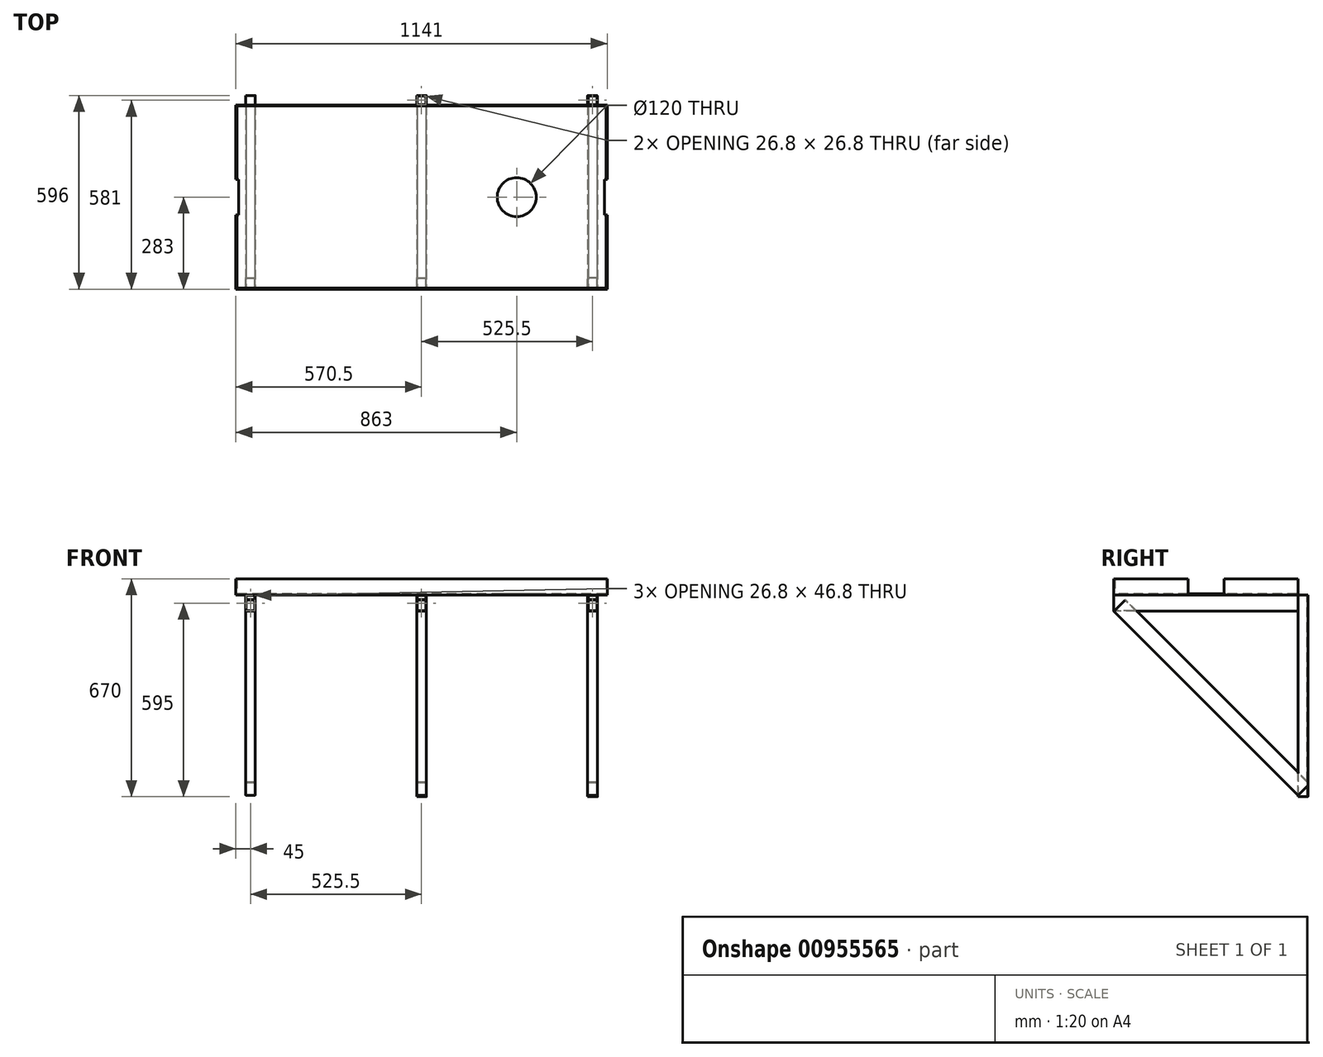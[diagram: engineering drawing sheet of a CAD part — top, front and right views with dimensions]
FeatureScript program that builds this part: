
annotation { "Feature Type Name" : "Feature", "Feature Type Description" : "" }
export const myFeature = defineFeature(function(context is Context, id is Id, definition is map)
    precondition{}
    {
        {
            var Q0;
            Q0=qCreatedBy(makeId("Top.planeOp"),FACE);
            var sketch = newSketch(context, id + "F0", { "sketchPlane" : qUnion([Q0])});
            skLineSegment(sketch, "E0.bottom", {"start": v(567.5, 280) * mm, "end": v(-567.5, 280) * mm});
            skLineSegment(sketch, "E0.top", {"start": v(567.5, -280) * mm, "end": v(-567.5, -280) * mm});
            skLineSegment(sketch, "E0.left", {"start": v(567.5, 280) * mm, "end": v(567.5, -280) * mm});
            skLineSegment(sketch, "E0.right", {"start": v(-567.5, 280) * mm, "end": v(-567.5, -280) * mm});
            skPoint(sketch, "E0.middle", {"position": v(0, 0) * mm});
            skLineSegment(sketch, "E1.0", {"start": v(570.5, 283) * mm, "end": v(-570.5, 283) * mm});
            skLineSegment(sketch, "E1.1", {"start": v(570.5, 283) * mm, "end": v(570.5, -283) * mm});
            skLineSegment(sketch, "E1.2", {"start": v(570.5, -283) * mm, "end": v(-570.5, -283) * mm});
            skLineSegment(sketch, "E1.3", {"start": v(-570.5, 283) * mm, "end": v(-570.5, -283) * mm});
            skLineSegment(sketch, "E2.bottom", {"start": v(567.5, 55) * mm, "end": v(-567.5, 55) * mm, "construction": true});
            skLineSegment(sketch, "E2.top", {"start": v(567.5, -55) * mm, "end": v(-567.5, -55) * mm, "construction": true});
            skLineSegment(sketch, "E2.left", {"start": v(567.5, 55) * mm, "end": v(567.5, -55) * mm, "construction": true});
            skLineSegment(sketch, "E2.right", {"start": v(-567.5, 55) * mm, "end": v(-567.5, -55) * mm, "construction": true});
            skLineSegment(sketch, "E3.bottom", {"start": v(-567.5, -55) * mm, "end": v(-562.5, -55) * mm});
            skLineSegment(sketch, "E3.top", {"start": v(-567.5, 55) * mm, "end": v(-562.5, 55) * mm});
            skLineSegment(sketch, "E3.left", {"start": v(-567.5, -55) * mm, "end": v(-567.5, 55) * mm});
            skLineSegment(sketch, "E3.right", {"start": v(-562.5, -55) * mm, "end": v(-562.5, 55) * mm});
            skLineSegment(sketch, "E4.MirrorCS", {"start": v(562.5, -55) * mm, "end": v(562.5, 55) * mm});
            skLineSegment(sketch, "E5", {"start": v(-567.5, -55) * mm, "end": v(-570.5, -55) * mm});
            skLineSegment(sketch, "E6", {"start": v(-567.5, 55) * mm, "end": v(-570.5, 55) * mm});
            skLineSegment(sketch, "E7.MirrorCS", {"start": v(567.5, -55) * mm, "end": v(570.5, -55) * mm});
            skLineSegment(sketch, "E8.MirrorCS", {"start": v(567.5, 55) * mm, "end": v(570.5, 55) * mm});
            skLineSegment(sketch, "E9", {"start": v(562.5, -55) * mm, "end": v(567.5, -55) * mm});
            skLineSegment(sketch, "E10", {"start": v(562.5, 55) * mm, "end": v(567.5, 55) * mm});
            skLineSegment(sketch, "E11", {"start": v(-567.5, 0) * mm, "end": v(562.5, 0) * mm, "construction": true});
            skCircle(sketch, "E12", {"center": v(292.5, 0) * mm, "radius": 60 * mm});
            skPoint(sketch, "E13", {"position": v(-540.5, 283) * mm});
            skLineSegment(sketch, "E14.bottom", {"start": v(-538.5, 283) * mm, "end": v(-512.5, 283) * mm});
            skLineSegment(sketch, "E14.top", {"start": v(-538.5, 313) * mm, "end": v(-512.5, 313) * mm});
            skLineSegment(sketch, "E14.left", {"start": v(-540.5, 285) * mm, "end": v(-540.5, 311) * mm});
            skLineSegment(sketch, "E14.right", {"start": v(-510.5, 285) * mm, "end": v(-510.5, 311) * mm});
            skLineSegment(sketch, "E15.0", {"start": v(-538.9, 286.6) * mm, "end": v(-538.9, 309.4) * mm});
            skLineSegment(sketch, "E15.1", {"start": v(-536.9, 311.4) * mm, "end": v(-514.1, 311.4) * mm});
            skLineSegment(sketch, "E15.2", {"start": v(-512.1, 286.6) * mm, "end": v(-512.1, 309.4) * mm});
            skLineSegment(sketch, "E16", {"start": v(-536.9, 284.6) * mm, "end": v(-514.1, 284.6) * mm});
            skPoint(sketch, "E17.visualSharp", {"position": v(-538.9, 311.4) * mm});
            skArc(sketch, "E17.filletArc", {"start": v(-536.9, 311.4) * mm, "mid": v(-538.31, 310.81) * mm, "end": v(-538.9, 309.4) * mm});
            skPoint(sketch, "E18.visualSharp", {"position": v(-512.1, 311.4) * mm});
            skArc(sketch, "E18.filletArc", {"start": v(-512.1, 309.4) * mm, "mid": v(-512.69, 310.81) * mm, "end": v(-514.1, 311.4) * mm});
            skPoint(sketch, "E19.visualSharp", {"position": v(-512.1, 284.6) * mm});
            skArc(sketch, "E19.filletArc", {"start": v(-514.1, 284.6) * mm, "mid": v(-512.69, 285.19) * mm, "end": v(-512.1, 286.6) * mm});
            skPoint(sketch, "E20.visualSharp", {"position": v(-538.9, 284.6) * mm});
            skArc(sketch, "E20.filletArc", {"start": v(-538.9, 286.6) * mm, "mid": v(-538.31, 285.19) * mm, "end": v(-536.9, 284.6) * mm});
            skPoint(sketch, "E21.visualSharp", {"position": v(-540.5, 313) * mm});
            skArc(sketch, "E21.filletArc", {"start": v(-538.5, 313) * mm, "mid": v(-539.91, 312.41) * mm, "end": v(-540.5, 311) * mm});
            skPoint(sketch, "E22.visualSharp", {"position": v(-510.5, 313) * mm});
            skArc(sketch, "E22.filletArc", {"start": v(-510.5, 311) * mm, "mid": v(-511.09, 312.41) * mm, "end": v(-512.5, 313) * mm});
            skPoint(sketch, "E23.visualSharp", {"position": v(-510.5, 283) * mm});
            skArc(sketch, "E23.filletArc", {"start": v(-512.5, 283) * mm, "mid": v(-511.09, 283.59) * mm, "end": v(-510.5, 285) * mm});
            skArc(sketch, "E24.filletArc", {"start": v(-540.5, 285) * mm, "mid": v(-539.91, 283.59) * mm, "end": v(-538.5, 283) * mm});
            skLineSegment(sketch, "E25.MirrorCS", {"start": v(538.5, 313) * mm, "end": v(512.5, 313) * mm});
            skLineSegment(sketch, "E26.MirrorCS", {"start": v(536.9, 311.4) * mm, "end": v(514.1, 311.4) * mm});
            skLineSegment(sketch, "E27.MirrorCS", {"start": v(536.9, 284.6) * mm, "end": v(514.1, 284.6) * mm});
            skLineSegment(sketch, "E28.MirrorCS", {"start": v(510.5, 285) * mm, "end": v(510.5, 311) * mm});
            skLineSegment(sketch, "E29.MirrorCS", {"start": v(512.1, 286.6) * mm, "end": v(512.1, 309.4) * mm});
            skLineSegment(sketch, "E30.MirrorCS", {"start": v(538.9, 286.6) * mm, "end": v(538.9, 309.4) * mm});
            skLineSegment(sketch, "E31.MirrorCS", {"start": v(540.5, 285) * mm, "end": v(540.5, 311) * mm});
            skArc(sketch, "E32.MirrorCS", {"start": v(512.1, 309.4) * mm, "mid": v(512.69, 310.81) * mm, "end": v(514.1, 311.4) * mm});
            skArc(sketch, "E33.MirrorCS", {"start": v(510.5, 311) * mm, "mid": v(511.09, 312.41) * mm, "end": v(512.5, 313) * mm});
            skArc(sketch, "E34.MirrorCS", {"start": v(536.9, 311.4) * mm, "mid": v(538.31, 310.81) * mm, "end": v(538.9, 309.4) * mm});
            skArc(sketch, "E35.MirrorCS", {"start": v(538.5, 313) * mm, "mid": v(539.91, 312.41) * mm, "end": v(540.5, 311) * mm});
            skArc(sketch, "E36.MirrorCS", {"start": v(512.5, 283) * mm, "mid": v(511.09, 283.59) * mm, "end": v(510.5, 285) * mm});
            skArc(sketch, "E37.MirrorCS", {"start": v(514.1, 284.6) * mm, "mid": v(512.69, 285.19) * mm, "end": v(512.1, 286.6) * mm});
            skArc(sketch, "E38.MirrorCS", {"start": v(538.9, 286.6) * mm, "mid": v(538.31, 285.19) * mm, "end": v(536.9, 284.6) * mm});
            skArc(sketch, "E39.MirrorCS", {"start": v(540.5, 285) * mm, "mid": v(539.91, 283.59) * mm, "end": v(538.5, 283) * mm});
            skLineSegment(sketch, "E40.1.0.0", {"start": v(-13, 313) * mm, "end": v(13, 313) * mm});
            skPoint(sketch, "E40.1.0.1", {"position": v(-13.4, 284.6) * mm});
            skLineSegment(sketch, "E40.1.0.2", {"start": v(13.4, 286.6) * mm, "end": v(13.4, 309.4) * mm});
            skLineSegment(sketch, "E40.1.0.3", {"start": v(-13.4, 286.6) * mm, "end": v(-13.4, 309.4) * mm});
            skPoint(sketch, "E40.1.0.4", {"position": v(13.4, 284.6) * mm});
            skPoint(sketch, "E40.1.0.5", {"position": v(-15, 313) * mm});
            skLineSegment(sketch, "E40.1.0.6", {"start": v(-15, 285) * mm, "end": v(-15, 311) * mm});
            skPoint(sketch, "E40.1.0.7", {"position": v(13.4, 311.4) * mm});
            skLineSegment(sketch, "E40.1.0.8", {"start": v(-11.4, 284.6) * mm, "end": v(11.4, 284.6) * mm});
            skPoint(sketch, "E40.1.0.9", {"position": v(15, 313) * mm});
            skLineSegment(sketch, "E40.1.0.10", {"start": v(15, 285) * mm, "end": v(15, 311) * mm});
            skLineSegment(sketch, "E40.1.0.11", {"start": v(-13, 283) * mm, "end": v(13, 283) * mm});
            skLineSegment(sketch, "E40.1.0.12", {"start": v(-11.4, 311.4) * mm, "end": v(11.4, 311.4) * mm});
            skPoint(sketch, "E40.1.0.13", {"position": v(-13.4, 311.4) * mm});
            skArc(sketch, "E40.1.0.14", {"start": v(13.4, 309.4) * mm, "mid": v(12.81, 310.81) * mm, "end": v(11.4, 311.4) * mm});
            skArc(sketch, "E40.1.0.15", {"start": v(15, 311) * mm, "mid": v(14.41, 312.41) * mm, "end": v(13, 313) * mm});
            skArc(sketch, "E40.1.0.16", {"start": v(-13, 313) * mm, "mid": v(-14.41, 312.41) * mm, "end": v(-15, 311) * mm});
            skArc(sketch, "E40.1.0.17", {"start": v(-13.4, 286.6) * mm, "mid": v(-12.81, 285.19) * mm, "end": v(-11.4, 284.6) * mm});
            skArc(sketch, "E40.1.0.18", {"start": v(-15, 285) * mm, "mid": v(-14.41, 283.59) * mm, "end": v(-13, 283) * mm});
            skArc(sketch, "E40.1.0.19", {"start": v(11.4, 284.6) * mm, "mid": v(12.81, 285.19) * mm, "end": v(13.4, 286.6) * mm});
            skArc(sketch, "E40.1.0.20", {"start": v(-11.4, 311.4) * mm, "mid": v(-12.81, 310.81) * mm, "end": v(-13.4, 309.4) * mm});
            skArc(sketch, "E40.1.0.21", {"start": v(13, 283) * mm, "mid": v(14.41, 283.59) * mm, "end": v(15, 285) * mm});
            skLineSegment(sketch, "E40.direction1", {"start": v(-538.5, 283) * mm, "end": v(-13, 283) * mm, "construction": true});
            skPoint(sketch, "E41", {"position": v(525.5, 284.6) * mm});
            skLineSegment(sketch, "E42.bottom", {"start": v(-540.5, 313) * mm, "end": v(-510.5, 313) * mm});
            skLineSegment(sketch, "E42.top", {"start": v(-540.5, 333) * mm, "end": v(-510.5, 333) * mm});
            skLineSegment(sketch, "E42.left", {"start": v(-540.5, 313) * mm, "end": v(-540.5, 333) * mm});
            skLineSegment(sketch, "E42.right", {"start": v(-510.5, 313) * mm, "end": v(-510.5, 333) * mm});
            skLineSegment(sketch, "E43.MirrorCS", {"start": v(540.5, 333) * mm, "end": v(510.5, 333) * mm});
            skLineSegment(sketch, "E44.MirrorCS", {"start": v(510.5, 313) * mm, "end": v(510.5, 333) * mm});
            skLineSegment(sketch, "E45.MirrorCS", {"start": v(540.5, 313) * mm, "end": v(540.5, 333) * mm});
            skLineSegment(sketch, "E46.MirrorCS", {"start": v(540.5, 313) * mm, "end": v(510.5, 313) * mm});
            skLineSegment(sketch, "E47.bottom", {"start": v(-15, 313) * mm, "end": v(15, 313) * mm});
            skLineSegment(sketch, "E47.top", {"start": v(-15, 333) * mm, "end": v(15, 333) * mm});
            skLineSegment(sketch, "E47.left", {"start": v(-15, 313) * mm, "end": v(-15, 333) * mm});
            skLineSegment(sketch, "E47.right", {"start": v(15, 313) * mm, "end": v(15, 333) * mm});
            skSolve(sketch);
        }
        {
            var Q0;
            Q0=makeQuery(id+"F0.imprint","IMPRINT",FACE,{"disambiguationData":[TD([[makeQuery(id+"F0.imprint","IMPRINT",EDGE,{"derivedFrom":sQuery(id+"F0.wireOp",EDGE,"E0.bottom")}),1.0]])]});
            extrude(context, id + "F1", {"entities" : qUnion([Q0]), "depth" : 4 * mm, "offsetDistance" : 25 * mm});
        }
        {
            var Q0;
            Q0=makeQuery(id+"F0.imprint","IMPRINT",FACE,{"disambiguationData":[TD([[makeQuery(id+"F0.imprint","IMPRINT",EDGE,{"derivedFrom":sQuery(id+"F0.wireOp",EDGE,"E0.bottom")}),-1.0]])]});
            var Q1;
            {var subQ4=sQuery(id+"F0.wireOp",EDGE,"E0.top");Q1=makeQuery(id+"F0.imprint","IMPRINT",FACE,{"disambiguationData":[TD([[makeQuery(id+"F0.imprint","IMPRINT",EDGE,{"derivedFrom":subQ4}),1.0]])]});}
            extrude(context, id + "F2", {"entities" : qUnion([Q0, Q1]), "operationType" : NewBodyOperationType.ADD, "depth" : 50 * mm, "offsetDistance" : 25 * mm});
        }
        {
            var Q0;
            Q0=makeQuery(id+"F2.opExtrude","SWEPT_FACE",FACE,{"disambiguationData":[OSD([sQuery(id+"F0.wireOp",EDGE,"E1.2")])]});
            var sketch = newSketch(context, id + "F3", { "sketchPlane" : qUnion([Q0])});
            skPoint(sketch, "E48", {"position": v(-540.5, 0) * mm});
            skLineSegment(sketch, "E49.bottom", {"start": v(-538.5, 0) * mm, "end": v(-512.5, 0) * mm});
            skLineSegment(sketch, "E49.top", {"start": v(-538.5, -50) * mm, "end": v(-512.5, -50) * mm});
            skLineSegment(sketch, "E49.left", {"start": v(-540.5, -2) * mm, "end": v(-540.5, -48) * mm});
            skLineSegment(sketch, "E49.right", {"start": v(-510.5, -2) * mm, "end": v(-510.5, -48) * mm});
            skLineSegment(sketch, "E50.MirrorCS", {"start": v(538.5, -50) * mm, "end": v(512.5, -50) * mm});
            skLineSegment(sketch, "E51.MirrorCS", {"start": v(540.5, -2) * mm, "end": v(540.5, -48) * mm});
            skLineSegment(sketch, "E52.MirrorCS", {"start": v(510.5, -2) * mm, "end": v(510.5, -48) * mm});
            skLineSegment(sketch, "E53.MirrorCS", {"start": v(538.5, 0) * mm, "end": v(512.5, 0) * mm});
            skPoint(sketch, "E54", {"position": v(-15, 0) * mm});
            skLineSegment(sketch, "E55.bottom", {"start": v(-13, 0) * mm, "end": v(13, 0) * mm});
            skLineSegment(sketch, "E55.top", {"start": v(-13, -50) * mm, "end": v(13, -50) * mm});
            skLineSegment(sketch, "E55.left", {"start": v(-15, -2) * mm, "end": v(-15, -48) * mm});
            skLineSegment(sketch, "E55.right", {"start": v(15, -2) * mm, "end": v(15, -48) * mm});
            skPoint(sketch, "E56.visualSharp", {"position": v(-510.5, -50) * mm});
            skArc(sketch, "E56.filletArc", {"start": v(-512.5, -50) * mm, "mid": v(-511.09, -49.41) * mm, "end": v(-510.5, -48) * mm});
            skPoint(sketch, "E57.visualSharp", {"position": v(-540.5, -50) * mm});
            skArc(sketch, "E57.filletArc", {"start": v(-540.5, -48) * mm, "mid": v(-539.91, -49.41) * mm, "end": v(-538.5, -50) * mm});
            skPoint(sketch, "E58.visualSharp", {"position": v(-510.5, 0) * mm});
            skArc(sketch, "E58.filletArc", {"start": v(-510.5, -2) * mm, "mid": v(-511.09, -0.59) * mm, "end": v(-512.5, 0) * mm});
            skArc(sketch, "E59.filletArc", {"start": v(-538.5, 0) * mm, "mid": v(-539.91, -0.59) * mm, "end": v(-540.5, -2) * mm});
            skPoint(sketch, "E60.visualSharp", {"position": v(540.5, 0) * mm});
            skArc(sketch, "E60.filletArc", {"start": v(540.5, -2) * mm, "mid": v(539.91, -0.59) * mm, "end": v(538.5, 0) * mm});
            skPoint(sketch, "E61.visualSharp", {"position": v(510.5, 0) * mm});
            skArc(sketch, "E61.filletArc", {"start": v(512.5, 0) * mm, "mid": v(511.09, -0.59) * mm, "end": v(510.5, -2) * mm});
            skPoint(sketch, "E62.visualSharp", {"position": v(510.5, -50) * mm});
            skArc(sketch, "E62.filletArc", {"start": v(510.5, -48) * mm, "mid": v(511.09, -49.41) * mm, "end": v(512.5, -50) * mm});
            skPoint(sketch, "E63.visualSharp", {"position": v(540.5, -50) * mm});
            skArc(sketch, "E63.filletArc", {"start": v(538.5, -50) * mm, "mid": v(539.91, -49.41) * mm, "end": v(540.5, -48) * mm});
            skPoint(sketch, "E64.visualSharp", {"position": v(-15, -50) * mm});
            skArc(sketch, "E64.filletArc", {"start": v(-15, -48) * mm, "mid": v(-14.41, -49.41) * mm, "end": v(-13, -50) * mm});
            skPoint(sketch, "E65.visualSharp", {"position": v(15, -50) * mm});
            skArc(sketch, "E65.filletArc", {"start": v(13, -50) * mm, "mid": v(14.41, -49.41) * mm, "end": v(15, -48) * mm});
            skPoint(sketch, "E66.visualSharp", {"position": v(15, 0) * mm});
            skArc(sketch, "E66.filletArc", {"start": v(15, -2) * mm, "mid": v(14.41, -0.59) * mm, "end": v(13, 0) * mm});
            skArc(sketch, "E67.filletArc", {"start": v(-13, 0) * mm, "mid": v(-14.41, -0.59) * mm, "end": v(-15, -2) * mm});
            skLineSegment(sketch, "E68.0", {"start": v(-538.9, -2) * mm, "end": v(-538.9, -48) * mm});
            skArc(sketch, "E69.0", {"start": v(-538.9, -48) * mm, "mid": v(-538.78, -48.28) * mm, "end": v(-538.5, -48.4) * mm});
            skLineSegment(sketch, "E70.0", {"start": v(-538.5, -48.4) * mm, "end": v(-512.5, -48.4) * mm});
            skArc(sketch, "E71.0", {"start": v(-512.5, -48.4) * mm, "mid": v(-512.22, -48.28) * mm, "end": v(-512.1, -48) * mm});
            skLineSegment(sketch, "E72.0", {"start": v(-512.1, -2) * mm, "end": v(-512.1, -48) * mm});
            skArc(sketch, "E73.0", {"start": v(-512.1, -2) * mm, "mid": v(-512.22, -1.72) * mm, "end": v(-512.5, -1.6) * mm});
            skArc(sketch, "E74.0", {"start": v(-538.5, -1.6) * mm, "mid": v(-538.78, -1.72) * mm, "end": v(-538.9, -2) * mm});
            skLineSegment(sketch, "E75.0", {"start": v(-538.5, -1.6) * mm, "end": v(-512.5, -1.6) * mm});
            skLineSegment(sketch, "E76.MirrorCS", {"start": v(538.5, -48.4) * mm, "end": v(512.5, -48.4) * mm});
            skArc(sketch, "E77.MirrorCS", {"start": v(538.9, -48) * mm, "mid": v(538.78, -48.28) * mm, "end": v(538.5, -48.4) * mm});
            skLineSegment(sketch, "E78.MirrorCS", {"start": v(538.9, -2) * mm, "end": v(538.9, -48) * mm});
            skArc(sketch, "E79.MirrorCS", {"start": v(512.5, -48.4) * mm, "mid": v(512.22, -48.28) * mm, "end": v(512.1, -48) * mm});
            skLineSegment(sketch, "E80.MirrorCS", {"start": v(512.1, -2) * mm, "end": v(512.1, -48) * mm});
            skArc(sketch, "E81.MirrorCS", {"start": v(512.1, -2) * mm, "mid": v(512.22, -1.72) * mm, "end": v(512.5, -1.6) * mm});
            skLineSegment(sketch, "E82.MirrorCS", {"start": v(538.5, -1.6) * mm, "end": v(512.5, -1.6) * mm});
            skArc(sketch, "E83.MirrorCS", {"start": v(538.5, -1.6) * mm, "mid": v(538.78, -1.72) * mm, "end": v(538.9, -2) * mm});
            skLineSegment(sketch, "E84.0", {"start": v(-13.4, -2) * mm, "end": v(-13.4, -48) * mm});
            skLineSegment(sketch, "E85.0", {"start": v(-13, -1.6) * mm, "end": v(13, -1.6) * mm});
            skLineSegment(sketch, "E86.0", {"start": v(13.4, -2) * mm, "end": v(13.4, -48) * mm});
            skLineSegment(sketch, "E87.0", {"start": v(-13, -48.4) * mm, "end": v(13, -48.4) * mm});
            skArc(sketch, "E88.0", {"start": v(-13.4, -48) * mm, "mid": v(-13.28, -48.28) * mm, "end": v(-13, -48.4) * mm});
            skArc(sketch, "E89.0", {"start": v(13, -48.4) * mm, "mid": v(13.28, -48.28) * mm, "end": v(13.4, -48) * mm});
            skArc(sketch, "E90.0", {"start": v(13.4, -2) * mm, "mid": v(13.28, -1.72) * mm, "end": v(13, -1.6) * mm});
            skArc(sketch, "E91.0", {"start": v(-13, -1.6) * mm, "mid": v(-13.28, -1.72) * mm, "end": v(-13.4, -2) * mm});
            skSolve(sketch);
        }
        {
            var Q0;
            Q0 = qSketchRegion(id + "F3", true);
            extrude(context, id + "F4", {"entities" : qUnion([Q0]), "oppositeDirection" : true, "depth" : 566 * mm, "offsetDistance" : 25 * mm});
        }
        {
            var Q0;
            Q0=makeQuery(id+"F0.imprint","IMPRINT",FACE,{"disambiguationData":[TD([[makeQuery(id+"F0.imprint","IMPRINT",EDGE,{"derivedFrom":sQuery(id+"F0.wireOp",EDGE,"E14.bottom")}),1.0]])]});
            var Q1;
            Q1=makeQuery(id+"F0.imprint","IMPRINT",FACE,{"disambiguationData":[TD([[makeQuery(id+"F0.imprint","IMPRINT",EDGE,{"derivedFrom":sQuery(id+"F0.wireOp",EDGE,"E40.1.0.2")}),-1.0]])]});
            var Q2;
            Q2=makeQuery(id+"F0.imprint","IMPRINT",FACE,{"disambiguationData":[TD([[makeQuery(id+"F0.imprint","IMPRINT",EDGE,{"derivedFrom":sQuery(id+"F0.wireOp",EDGE,"E26.MirrorCS")}),-1.0]])]});
            extrude(context, id + "F5", {"entities" : qUnion([Q0, Q1, Q2]), "oppositeDirection" : true, "depth" : 620 * mm, "offsetDistance" : 25 * mm});
        }
        {
            var Q0;
            Q0=makeQuery(id+"F4.opExtrude","SWEPT_FACE",FACE,{"disambiguationData":[OSD([sQuery(id+"F3.wireOp",EDGE,"E49.top")])]});
            var sketch = newSketch(context, id + "F6", { "sketchPlane" : qUnion([Q0])});
            skPoint(sketch, "E92", {"position": v(-540.5, 283) * mm});
            skLineSegment(sketch, "E93.bottom", {"start": v(-538.5, 283) * mm, "end": v(-512.5, 283) * mm});
            skLineSegment(sketch, "E93.top", {"start": v(-538.5, 233) * mm, "end": v(-512.5, 233) * mm});
            skLineSegment(sketch, "E93.left", {"start": v(-540.5, 281) * mm, "end": v(-540.5, 235) * mm});
            skLineSegment(sketch, "E93.right", {"start": v(-510.5, 281) * mm, "end": v(-510.5, 235) * mm});
            skLineSegment(sketch, "E94.0", {"start": v(-536.9, 281.4) * mm, "end": v(-514.1, 281.4) * mm});
            skLineSegment(sketch, "E94.1", {"start": v(-538.9, 279.4) * mm, "end": v(-538.9, 236.6) * mm});
            skLineSegment(sketch, "E94.2", {"start": v(-536.9, 234.6) * mm, "end": v(-514.1, 234.6) * mm});
            skLineSegment(sketch, "E94.3", {"start": v(-512.1, 279.4) * mm, "end": v(-512.1, 236.6) * mm});
            skPoint(sketch, "E95.visualSharp", {"position": v(-538.9, 281.4) * mm});
            skArc(sketch, "E95.filletArc", {"start": v(-536.9, 281.4) * mm, "mid": v(-538.31, 280.81) * mm, "end": v(-538.9, 279.4) * mm});
            skPoint(sketch, "E96.visualSharp", {"position": v(-512.1, 281.4) * mm});
            skArc(sketch, "E96.filletArc", {"start": v(-512.1, 279.4) * mm, "mid": v(-512.69, 280.81) * mm, "end": v(-514.1, 281.4) * mm});
            skPoint(sketch, "E97.visualSharp", {"position": v(-510.5, 283) * mm});
            skArc(sketch, "E97.filletArc", {"start": v(-510.5, 281) * mm, "mid": v(-511.09, 282.41) * mm, "end": v(-512.5, 283) * mm});
            skArc(sketch, "E98.filletArc", {"start": v(-538.5, 283) * mm, "mid": v(-539.91, 282.41) * mm, "end": v(-540.5, 281) * mm});
            skPoint(sketch, "E99.visualSharp", {"position": v(-540.5, 233) * mm});
            skArc(sketch, "E99.filletArc", {"start": v(-540.5, 235) * mm, "mid": v(-539.91, 233.59) * mm, "end": v(-538.5, 233) * mm});
            skPoint(sketch, "E100.visualSharp", {"position": v(-538.9, 234.6) * mm});
            skArc(sketch, "E100.filletArc", {"start": v(-538.9, 236.6) * mm, "mid": v(-538.31, 235.19) * mm, "end": v(-536.9, 234.6) * mm});
            skPoint(sketch, "E101.visualSharp", {"position": v(-510.5, 233) * mm});
            skArc(sketch, "E101.filletArc", {"start": v(-512.5, 233) * mm, "mid": v(-511.09, 233.59) * mm, "end": v(-510.5, 235) * mm});
            skPoint(sketch, "E102.visualSharp", {"position": v(-512.1, 234.6) * mm});
            skArc(sketch, "E102.filletArc", {"start": v(-514.1, 234.6) * mm, "mid": v(-512.69, 235.19) * mm, "end": v(-512.1, 236.6) * mm});
            skArc(sketch, "E103.MirrorCS", {"start": v(512.5, 233) * mm, "mid": v(511.09, 233.59) * mm, "end": v(510.5, 235) * mm});
            skArc(sketch, "E104.MirrorCS", {"start": v(540.5, 235) * mm, "mid": v(539.91, 233.59) * mm, "end": v(538.5, 233) * mm});
            skArc(sketch, "E105.MirrorCS", {"start": v(510.5, 281) * mm, "mid": v(511.09, 282.41) * mm, "end": v(512.5, 283) * mm});
            skArc(sketch, "E106.MirrorCS", {"start": v(512.1, 279.4) * mm, "mid": v(512.69, 280.81) * mm, "end": v(514.1, 281.4) * mm});
            skArc(sketch, "E107.MirrorCS", {"start": v(538.5, 283) * mm, "mid": v(539.91, 282.41) * mm, "end": v(540.5, 281) * mm});
            skArc(sketch, "E108.MirrorCS", {"start": v(538.9, 236.6) * mm, "mid": v(538.31, 235.19) * mm, "end": v(536.9, 234.6) * mm});
            skArc(sketch, "E109.MirrorCS", {"start": v(536.9, 281.4) * mm, "mid": v(538.31, 280.81) * mm, "end": v(538.9, 279.4) * mm});
            skArc(sketch, "E110.MirrorCS", {"start": v(514.1, 234.6) * mm, "mid": v(512.69, 235.19) * mm, "end": v(512.1, 236.6) * mm});
            skPoint(sketch, "E111.MirrorP", {"position": v(540.5, 283) * mm});
            skPoint(sketch, "E112.MirrorP", {"position": v(512.1, 234.6) * mm});
            skLineSegment(sketch, "E113.MirrorCS", {"start": v(538.5, 233) * mm, "end": v(512.5, 233) * mm});
            skLineSegment(sketch, "E114.MirrorCS", {"start": v(510.5, 281) * mm, "end": v(510.5, 235) * mm});
            skPoint(sketch, "E115.MirrorP", {"position": v(538.9, 234.6) * mm});
            skPoint(sketch, "E116.MirrorP", {"position": v(510.5, 283) * mm});
            skLineSegment(sketch, "E117.MirrorCS", {"start": v(540.5, 281) * mm, "end": v(540.5, 235) * mm});
            skLineSegment(sketch, "E118.MirrorCS", {"start": v(538.9, 279.4) * mm, "end": v(538.9, 236.6) * mm});
            skPoint(sketch, "E119.MirrorP", {"position": v(512.1, 281.4) * mm});
            skLineSegment(sketch, "E120.MirrorCS", {"start": v(538.5, 283) * mm, "end": v(512.5, 283) * mm});
            skLineSegment(sketch, "E121.MirrorCS", {"start": v(512.1, 279.4) * mm, "end": v(512.1, 236.6) * mm});
            skPoint(sketch, "E122.MirrorP", {"position": v(510.5, 233) * mm});
            skLineSegment(sketch, "E123.MirrorCS", {"start": v(536.9, 234.6) * mm, "end": v(514.1, 234.6) * mm});
            skLineSegment(sketch, "E124.MirrorCS", {"start": v(536.9, 281.4) * mm, "end": v(514.1, 281.4) * mm});
            skPoint(sketch, "E125.MirrorP", {"position": v(540.5, 233) * mm});
            skPoint(sketch, "E126.MirrorP", {"position": v(538.9, 281.4) * mm});
            skPoint(sketch, "E127.1.0.0", {"position": v(15, 283) * mm});
            skPoint(sketch, "E127.1.0.1", {"position": v(-15, 233) * mm});
            skPoint(sketch, "E127.1.0.2", {"position": v(-13.4, 281.4) * mm});
            skLineSegment(sketch, "E127.1.0.3", {"start": v(-13, 283) * mm, "end": v(13, 283) * mm});
            skPoint(sketch, "E127.1.0.4", {"position": v(-13.4, 234.6) * mm});
            skPoint(sketch, "E127.1.0.5", {"position": v(15, 233) * mm});
            skPoint(sketch, "E127.1.0.6", {"position": v(13.4, 234.6) * mm});
            skPoint(sketch, "E127.1.0.7", {"position": v(13.4, 281.4) * mm});
            skLineSegment(sketch, "E127.1.0.8", {"start": v(-13, 233) * mm, "end": v(13, 233) * mm});
            skLineSegment(sketch, "E127.1.0.9", {"start": v(-15, 281) * mm, "end": v(-15, 235) * mm});
            skLineSegment(sketch, "E127.1.0.10", {"start": v(15, 281) * mm, "end": v(15, 235) * mm});
            skLineSegment(sketch, "E127.1.0.11", {"start": v(-11.4, 281.4) * mm, "end": v(11.4, 281.4) * mm});
            skLineSegment(sketch, "E127.1.0.12", {"start": v(-13.4, 279.4) * mm, "end": v(-13.4, 236.6) * mm});
            skLineSegment(sketch, "E127.1.0.13", {"start": v(-11.4, 234.6) * mm, "end": v(11.4, 234.6) * mm});
            skLineSegment(sketch, "E127.1.0.14", {"start": v(13.4, 279.4) * mm, "end": v(13.4, 236.6) * mm});
            skPoint(sketch, "E127.1.0.15", {"position": v(-15, 283) * mm});
            skPoint(sketch, "E127.1.0.16", {"position": v(-15, 283) * mm});
            skArc(sketch, "E127.1.0.17", {"start": v(-13.4, 236.6) * mm, "mid": v(-12.81, 235.19) * mm, "end": v(-11.4, 234.6) * mm});
            skArc(sketch, "E127.1.0.18", {"start": v(11.4, 234.6) * mm, "mid": v(12.81, 235.19) * mm, "end": v(13.4, 236.6) * mm});
            skArc(sketch, "E127.1.0.19", {"start": v(13, 233) * mm, "mid": v(14.41, 233.59) * mm, "end": v(15, 235) * mm});
            skArc(sketch, "E127.1.0.20", {"start": v(-11.4, 281.4) * mm, "mid": v(-12.81, 280.81) * mm, "end": v(-13.4, 279.4) * mm});
            skArc(sketch, "E127.1.0.21", {"start": v(13.4, 279.4) * mm, "mid": v(12.81, 280.81) * mm, "end": v(11.4, 281.4) * mm});
            skArc(sketch, "E127.1.0.22", {"start": v(15, 281) * mm, "mid": v(14.41, 282.41) * mm, "end": v(13, 283) * mm});
            skArc(sketch, "E127.1.0.23", {"start": v(-15, 235) * mm, "mid": v(-14.41, 233.59) * mm, "end": v(-13, 233) * mm});
            skArc(sketch, "E127.1.0.24", {"start": v(-13, 283) * mm, "mid": v(-14.41, 282.41) * mm, "end": v(-15, 281) * mm});
            skLineSegment(sketch, "E127.direction1", {"start": v(-540.5, 233) * mm, "end": v(-15, 233) * mm, "construction": true});
            skSolve(sketch);
        }
        {
            var Q0;
            Q0 = qSketchRegion(id + "F6", true);
            extrude(context, id + "F7", {"entities" : qUnion([Q0]), "depth" : 800.45 * mm, "offsetDistance" : 25 * mm});
        }
        {
            var Q0;
            Q0=makeQuery(id+"F7.opExtrude","SWEPT_BODY",BODY,{"disambiguationData":[OSD([sQuery(id+"F6.wireOp",EDGE,"E93.bottom"),sQuery(id+"F6.wireOp",EDGE,"E93.top"),sQuery(id+"F6.wireOp",EDGE,"E93.left"),sQuery(id+"F6.wireOp",EDGE,"E93.right"),sQuery(id+"F6.wireOp",EDGE,"E94.0"),sQuery(id+"F6.wireOp",EDGE,"E94.1"),sQuery(id+"F6.wireOp",EDGE,"E94.2"),sQuery(id+"F6.wireOp",EDGE,"E94.3"),sQuery(id+"F6.wireOp",EDGE,"E95.filletArc"),sQuery(id+"F6.wireOp",EDGE,"E96.filletArc"),sQuery(id+"F6.wireOp",EDGE,"E97.filletArc"),sQuery(id+"F6.wireOp",EDGE,"E98.filletArc"),sQuery(id+"F6.wireOp",EDGE,"E99.filletArc"),sQuery(id+"F6.wireOp",EDGE,"E100.filletArc"),sQuery(id+"F6.wireOp",EDGE,"E101.filletArc"),sQuery(id+"F6.wireOp",EDGE,"E102.filletArc")])]});
            var Q1;
            Q1=makeQuery(id+"F7.opExtrude","SWEPT_BODY",BODY,{"disambiguationData":[OSD([sQuery(id+"F6.wireOp",EDGE,"E127.1.0.3"),sQuery(id+"F6.wireOp",EDGE,"E127.1.0.8"),sQuery(id+"F6.wireOp",EDGE,"E127.1.0.9"),sQuery(id+"F6.wireOp",EDGE,"E127.1.0.10"),sQuery(id+"F6.wireOp",EDGE,"E127.1.0.11"),sQuery(id+"F6.wireOp",EDGE,"E127.1.0.12"),sQuery(id+"F6.wireOp",EDGE,"E127.1.0.13"),sQuery(id+"F6.wireOp",EDGE,"E127.1.0.14"),sQuery(id+"F6.wireOp",EDGE,"E127.1.0.17"),sQuery(id+"F6.wireOp",EDGE,"E127.1.0.18"),sQuery(id+"F6.wireOp",EDGE,"E127.1.0.19"),sQuery(id+"F6.wireOp",EDGE,"E127.1.0.20"),sQuery(id+"F6.wireOp",EDGE,"E127.1.0.21"),sQuery(id+"F6.wireOp",EDGE,"E127.1.0.22"),sQuery(id+"F6.wireOp",EDGE,"E127.1.0.23"),sQuery(id+"F6.wireOp",EDGE,"E127.1.0.24")])]});
            var Q2;
            Q2=makeQuery(id+"F7.opExtrude","SWEPT_BODY",BODY,{"disambiguationData":[OSD([sQuery(id+"F6.wireOp",EDGE,"E103.MirrorCS"),sQuery(id+"F6.wireOp",EDGE,"E104.MirrorCS"),sQuery(id+"F6.wireOp",EDGE,"E105.MirrorCS"),sQuery(id+"F6.wireOp",EDGE,"E106.MirrorCS"),sQuery(id+"F6.wireOp",EDGE,"E107.MirrorCS"),sQuery(id+"F6.wireOp",EDGE,"E108.MirrorCS"),sQuery(id+"F6.wireOp",EDGE,"E109.MirrorCS"),sQuery(id+"F6.wireOp",EDGE,"E110.MirrorCS"),sQuery(id+"F6.wireOp",EDGE,"E113.MirrorCS"),sQuery(id+"F6.wireOp",EDGE,"E114.MirrorCS"),sQuery(id+"F6.wireOp",EDGE,"E117.MirrorCS"),sQuery(id+"F6.wireOp",EDGE,"E118.MirrorCS"),sQuery(id+"F6.wireOp",EDGE,"E120.MirrorCS"),sQuery(id+"F6.wireOp",EDGE,"E121.MirrorCS"),sQuery(id+"F6.wireOp",EDGE,"E123.MirrorCS"),sQuery(id+"F6.wireOp",EDGE,"E124.MirrorCS")])]});
            var Q3;
            Q3=makeQuery(id+"F4.opExtrude","CAP_EDGE",EDGE,{"disambiguationData":[OSD([sQuery(id+"F3.wireOp",EDGE,"E49.top")])],"isStart":true});
            transform(context, id + "F8", {"entities" : qUnion([Q0, Q1, Q2]), "transformType" : TransformType.ROTATION, "transformAxis" : qUnion([Q3]), "angle" : 45 * degree, "makeCopy" : false});
        }
        {
            var Q0;
            Q0=makeQuery(id+"F0.imprint","IMPRINT",FACE,{"disambiguationData":[TD([[makeQuery(id+"F0.imprint","IMPRINT",EDGE,{"derivedFrom":sQuery(id+"F0.wireOp",EDGE,"E43.MirrorCS")}),1.0]])]});
            var Q1;
            Q1=makeQuery(id+"F0.imprint","IMPRINT",FACE,{"disambiguationData":[TD([[makeQuery(id+"F0.imprint","IMPRINT",EDGE,{"derivedFrom":sQuery(id+"F0.wireOp",EDGE,"E47.top")}),-1.0]])]});
            var Q2;
            Q2=makeQuery(id+"F0.imprint","IMPRINT",FACE,{"disambiguationData":[TD([[makeQuery(id+"F0.imprint","IMPRINT",EDGE,{"derivedFrom":sQuery(id+"F0.wireOp",EDGE,"E42.top")}),-1.0]])]});
            extrude(context, id + "F9", {"entities" : qUnion([Q0, Q1, Q2]), "operationType" : NewBodyOperationType.REMOVE, "oppositeDirection" : true, "depth" : 620 * mm, "offsetDistance" : 25 * mm});
        }
    });
